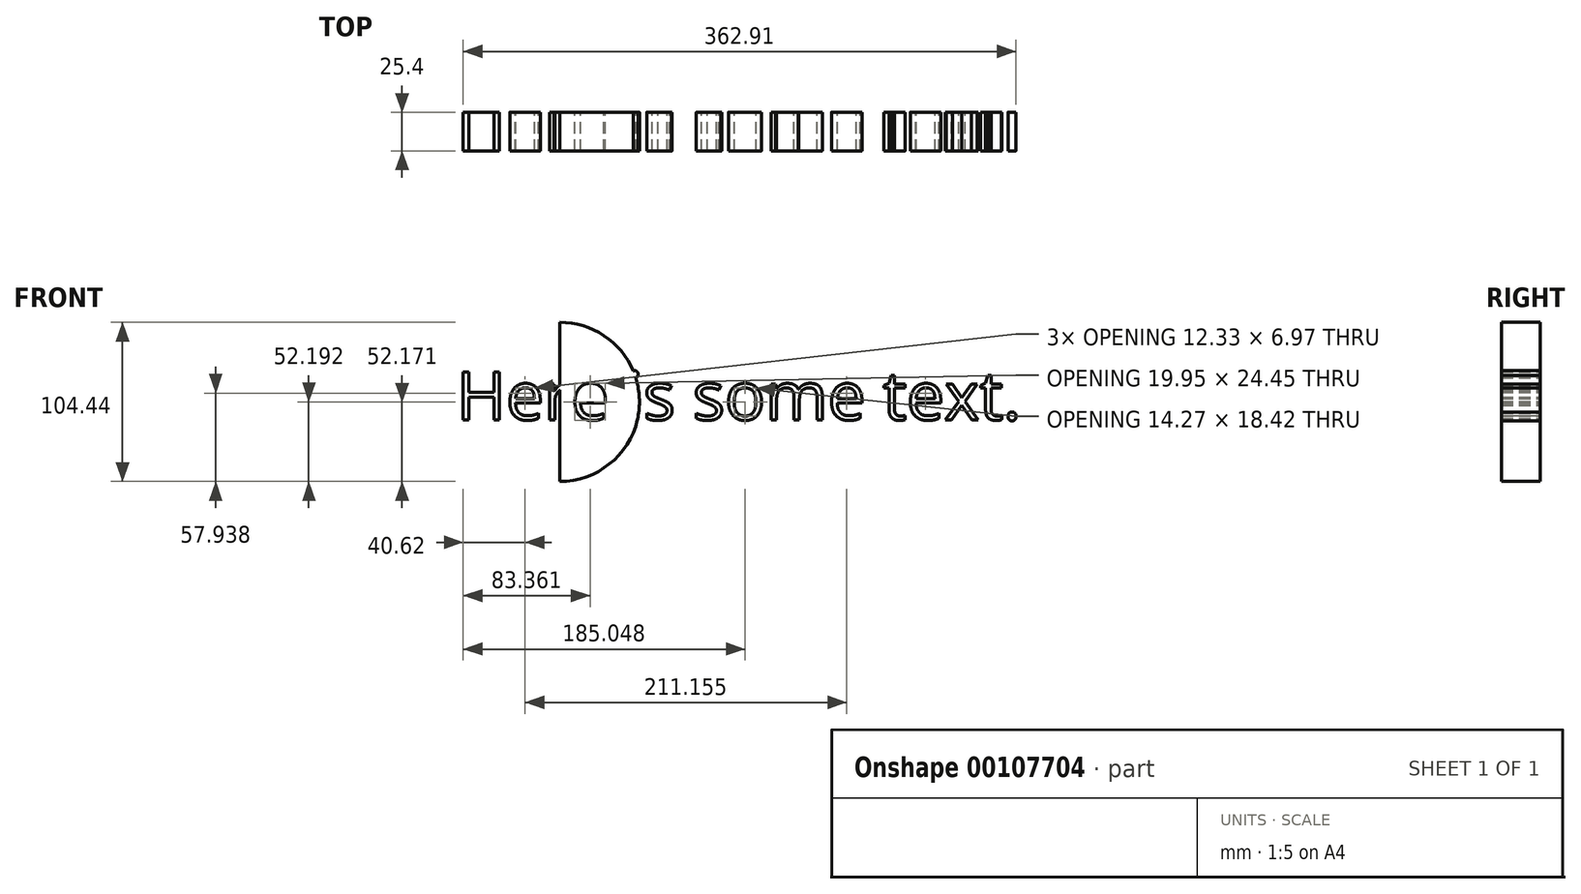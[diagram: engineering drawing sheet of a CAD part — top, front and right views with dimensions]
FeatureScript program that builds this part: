
annotation { "Feature Type Name" : "Feature", "Feature Type Description" : "" }
export const myFeature = defineFeature(function(context is Context, id is Id, definition is map)
    precondition{}
    {
        {
            var Q0;
            Q0=qCreatedBy(makeId("Front.planeOp"),FACE);
            var sketch = newSketch(context, id + "F0", { "sketchPlane" : qUnion([Q0])});
            skArc(sketch, "E0", {"start": v(0, 52.22) * mm, "mid": v(52.22, 0) * mm, "end": v(0, -52.22) * mm});
            skLineSegment(sketch, "E1", {"start": v(0, 52.22) * mm, "end": v(0, -52.22) * mm});
            skText(sketch, "E2", { "text": "Here is some text.", "fontName": "OpenSans-Regular.ttf"});
            skPoint(sketch, "E3", {"position": v(10.67, 38.62) * mm});
            skPoint(sketch, "E4", {"position": v(23.35, 31.17) * mm});
            skPoint(sketch, "E5", {"position": v(10.03, 23.25) * mm});
            const initialGuessF0  = {"E2": [-0.0678, -0.01182, 1, 0, 0.03173]};
            skSetInitialGuess(sketch, initialGuessF0);
            skSolve(sketch);
        }
        {
            var Q0;
            Q0 = qSketchRegion(id + "F0", true);
            extrude(context, id + "F1", {"entities" : qUnion([Q0]), "depth" : 25.4 * mm});
        }
    });
